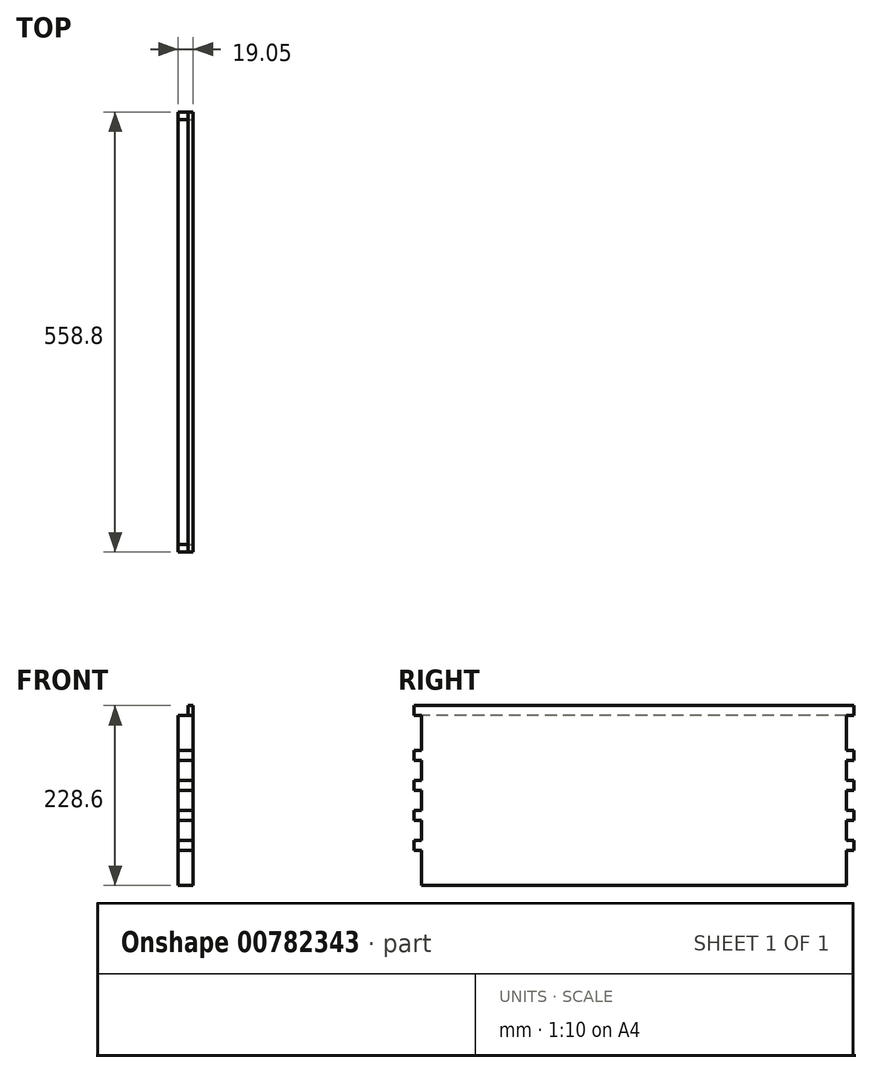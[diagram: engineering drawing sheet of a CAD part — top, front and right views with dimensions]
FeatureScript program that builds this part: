
annotation { "Feature Type Name" : "Feature", "Feature Type Description" : "" }
export const myFeature = defineFeature(function(context is Context, id is Id, definition is map)
    precondition{}
    {
        {
            var Q0;
            Q0=qCreatedBy(makeId("Right.planeOp"),FACE);
            var sketch = newSketch(context, id + "F0", { "sketchPlane" : qUnion([Q0])});
            skLineSegment(sketch, "E0.bottom", {"start": v(279.4, -114.3) * mm, "end": v(-279.4, -114.3) * mm});
            skLineSegment(sketch, "E0.top", {"start": v(279.4, 114.3) * mm, "end": v(-279.4, 114.3) * mm});
            skLineSegment(sketch, "E0.left", {"start": v(279.4, -114.3) * mm, "end": v(279.4, 114.3) * mm});
            skLineSegment(sketch, "E0.right", {"start": v(-279.4, -114.3) * mm, "end": v(-279.4, 114.3) * mm});
            skPoint(sketch, "E0.middle", {"position": v(0, 0) * mm});
            skSolve(sketch);
        }
        {
            var Q0;
            Q0 = qSketchRegion(id + "F0", true);
            extrude(context, id + "F1", {"entities" : qUnion([Q0]), "depth" : 19.05 * mm, "offsetDistance" : 25.4 * mm});
        }
        {
            var Q0;
            Q0=makeQuery(id+"F1.opExtrude","SWEPT_FACE",FACE,{"disambiguationData":[OSD([sQuery(id+"F0.wireOp",EDGE,"E0.right")])]});
            var sketch = newSketch(context, id + "F2", { "sketchPlane" : qUnion([Q0])});
            skLineSegment(sketch, "E1.bottom", {"start": v(0, 114.3) * mm, "end": v(12.7, 114.3) * mm});
            skLineSegment(sketch, "E1.top", {"start": v(0, 101.6) * mm, "end": v(12.7, 101.6) * mm});
            skLineSegment(sketch, "E1.left", {"start": v(0, 114.3) * mm, "end": v(0, 101.6) * mm});
            skLineSegment(sketch, "E1.right", {"start": v(12.7, 114.3) * mm, "end": v(12.7, 101.6) * mm});
            skSolve(sketch);
        }
        {
            var Q0;
            Q0 = qSketchRegion(id + "F2", true);
            extrude(context, id + "F3", {"entities" : qUnion([Q0]), "operationType" : NewBodyOperationType.REMOVE, "endBound" : BoundingType.UP_TO_NEXT, "oppositeDirection" : true, "depth" : 25.4 * mm, "offsetDistance" : 25.4 * mm});
        }
        {
            var Q0;
            Q0=makeQuery(id+"F1.opExtrude","CAP_FACE",FACE,{"disambiguationData":[OSD([sQuery(id+"F0.wireOp",EDGE,"E0.bottom"),sQuery(id+"F0.wireOp",EDGE,"E0.top"),sQuery(id+"F0.wireOp",EDGE,"E0.left"),sQuery(id+"F0.wireOp",EDGE,"E0.right")])],"isStart":false});
            var sketch = newSketch(context, id + "F4", { "sketchPlane" : qUnion([Q0])});
            skLineSegment(sketch, "E2", {"start": v(0, 114.3) * mm, "end": v(0, -114.3) * mm});
            skLineSegment(sketch, "E3.bottom", {"start": v(-279.4, 101.6) * mm, "end": v(-269.88, 101.6) * mm});
            skLineSegment(sketch, "E3.top", {"start": v(-279.4, 57.15) * mm, "end": v(-269.88, 57.15) * mm});
            skLineSegment(sketch, "E3.left", {"start": v(-279.4, 114.3) * mm, "end": v(-279.4, 57.15) * mm});
            skLineSegment(sketch, "E3.right", {"start": v(-269.88, 101.6) * mm, "end": v(-269.88, 57.15) * mm});
            skLineSegment(sketch, "E4.bottom", {"start": v(-279.4, 44.45) * mm, "end": v(-269.88, 44.45) * mm});
            skLineSegment(sketch, "E4.top", {"start": v(-279.4, 19.05) * mm, "end": v(-269.88, 19.05) * mm});
            skLineSegment(sketch, "E4.left", {"start": v(-279.4, 44.45) * mm, "end": v(-279.4, 19.05) * mm});
            skLineSegment(sketch, "E4.right", {"start": v(-269.88, 44.45) * mm, "end": v(-269.88, 19.05) * mm});
            skLineSegment(sketch, "E5.bottom", {"start": v(-279.4, 6.35) * mm, "end": v(-269.88, 6.35) * mm});
            skLineSegment(sketch, "E5.top", {"start": v(-279.4, -19.05) * mm, "end": v(-269.88, -19.05) * mm});
            skLineSegment(sketch, "E5.left", {"start": v(-279.4, 6.35) * mm, "end": v(-279.4, -19.05) * mm});
            skLineSegment(sketch, "E5.right", {"start": v(-269.88, 6.35) * mm, "end": v(-269.88, -19.05) * mm});
            skLineSegment(sketch, "E6.bottom", {"start": v(-279.4, -31.75) * mm, "end": v(-269.88, -31.75) * mm});
            skLineSegment(sketch, "E6.top", {"start": v(-279.4, -57.15) * mm, "end": v(-269.88, -57.15) * mm});
            skLineSegment(sketch, "E6.left", {"start": v(-279.4, -31.75) * mm, "end": v(-279.4, -57.15) * mm});
            skLineSegment(sketch, "E6.right", {"start": v(-269.88, -31.75) * mm, "end": v(-269.88, -57.15) * mm});
            skLineSegment(sketch, "E7.bottom", {"start": v(-279.4, -69.85) * mm, "end": v(-269.88, -69.85) * mm});
            skLineSegment(sketch, "E7.top", {"start": v(-279.4, -114.3) * mm, "end": v(-269.88, -114.3) * mm});
            skLineSegment(sketch, "E7.left", {"start": v(-279.4, -69.85) * mm, "end": v(-279.4, -114.3) * mm});
            skLineSegment(sketch, "E7.right", {"start": v(-269.88, -69.85) * mm, "end": v(-269.88, -114.3) * mm});
            skLineSegment(sketch, "E8.MirrorCS", {"start": v(279.4, 114.3) * mm, "end": v(279.4, 57.15) * mm});
            skLineSegment(sketch, "E9.MirrorCS", {"start": v(279.4, 101.6) * mm, "end": v(269.88, 101.6) * mm});
            skLineSegment(sketch, "E10.MirrorCS", {"start": v(269.88, 101.6) * mm, "end": v(269.88, 57.15) * mm});
            skLineSegment(sketch, "E11.MirrorCS", {"start": v(279.4, 57.15) * mm, "end": v(269.88, 57.15) * mm});
            skLineSegment(sketch, "E12.MirrorCS", {"start": v(279.4, 44.45) * mm, "end": v(279.4, 19.05) * mm});
            skLineSegment(sketch, "E13.MirrorCS", {"start": v(279.4, 44.45) * mm, "end": v(269.88, 44.45) * mm});
            skLineSegment(sketch, "E14.MirrorCS", {"start": v(269.88, 44.45) * mm, "end": v(269.88, 19.05) * mm});
            skLineSegment(sketch, "E15.MirrorCS", {"start": v(279.4, 19.05) * mm, "end": v(269.88, 19.05) * mm});
            skLineSegment(sketch, "E16.MirrorCS", {"start": v(279.4, 6.35) * mm, "end": v(269.88, 6.35) * mm});
            skLineSegment(sketch, "E17.MirrorCS", {"start": v(279.4, 6.35) * mm, "end": v(279.4, -19.05) * mm});
            skLineSegment(sketch, "E18.MirrorCS", {"start": v(279.4, -19.05) * mm, "end": v(269.88, -19.05) * mm});
            skLineSegment(sketch, "E19.MirrorCS", {"start": v(269.88, 6.35) * mm, "end": v(269.88, -19.05) * mm});
            skLineSegment(sketch, "E20.MirrorCS", {"start": v(279.4, -31.75) * mm, "end": v(269.88, -31.75) * mm});
            skLineSegment(sketch, "E21.MirrorCS", {"start": v(279.4, -31.75) * mm, "end": v(279.4, -57.15) * mm});
            skLineSegment(sketch, "E22.MirrorCS", {"start": v(269.88, -31.75) * mm, "end": v(269.88, -57.15) * mm});
            skLineSegment(sketch, "E23.MirrorCS", {"start": v(279.4, -57.15) * mm, "end": v(269.88, -57.15) * mm});
            skLineSegment(sketch, "E24.MirrorCS", {"start": v(279.4, -114.3) * mm, "end": v(269.88, -114.3) * mm});
            skLineSegment(sketch, "E25.MirrorCS", {"start": v(279.4, -69.85) * mm, "end": v(279.4, -114.3) * mm});
            skLineSegment(sketch, "E26.MirrorCS", {"start": v(269.88, -69.85) * mm, "end": v(269.88, -114.3) * mm});
            skLineSegment(sketch, "E27.MirrorCS", {"start": v(279.4, -69.85) * mm, "end": v(269.88, -69.85) * mm});
            skSolve(sketch);
        }
        {
            var Q0;
            Q0 = qSketchRegion(id + "F4", true);
            extrude(context, id + "F5", {"entities" : qUnion([Q0]), "operationType" : NewBodyOperationType.REMOVE, "endBound" : BoundingType.UP_TO_NEXT, "oppositeDirection" : true, "depth" : 25.4 * mm, "offsetDistance" : 25.4 * mm});
        }
    });
